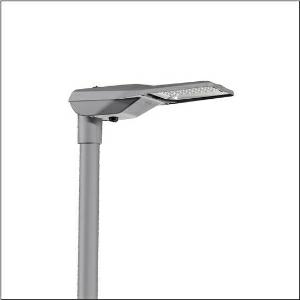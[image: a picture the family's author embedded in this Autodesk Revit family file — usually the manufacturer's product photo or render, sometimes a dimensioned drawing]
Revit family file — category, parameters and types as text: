
# Revit family: streetlight_sl_21_mini___st0_8a_5xe2c33t08hb_2b08
name_source: partatom
category: Lighting Fixtures
units: mm (PartAtom-declared; Revit-internal decimal feet)

## family parameters
Cut with Voids When Loaded = No
Host = Face
Light Source = No
Part Type = Normal
Room Calculation Point = No
Round Connector Dimension = Use Diameter
Shared = No

## types (1)
- --- (1 x LED, 9040 lm, 66 W, 3000K)
    Apparent Load = 66 VA
    CIE Flux Codes = 38 75 97 100 100
    Color Rendering = 70
    Color Temperature = 3000K
    Default Elevation = 1800 mm
    Description = Streetlight SL 21 mini, mast luminaire, primary light control with lens, of PMMA, primary optical cover: cover, of toughened safety glass, transparent, light distribution: ST0.8a, light emission: direct distribution, primary light characteristic: asymmetric, installation type: side-entry, post-top, LED, High Power LED, rated luminous flux: 9.040lm, luminous efficacy: 137lm/W, light colour: 730, colour temperature: 3000K, control gear: D4i, control: overheat protection, constant luminous flux control, time-dependent luminous flux control, flexible luminous flux parameterisation, pre-setting: logarithmic dimming characteristic, mains connection: 220..240V, AC, 50/60Hz, start of lifetime: 66W, end of service life: 69W, reduction: 30W, luminaire housing, of diecast aluminium, powder-coated, Siteco® metallic grey (DB 702S), corrosivity category C5 mid according to DIN EN ISO 12944, please order mast flange separately, inclination adjustable: 0°, 5°, 10°, 15°, sealing non-destructively replaceable, multi-level sealing system, length: 628mm, width: 235mm, height: 110mm, mast flange for spigot size: 42mm (side-entry): 5XC10008XM4, 60/48mm (side-entry/post-top): 5XC10108XM2, 76/60mm (side-entry/post-top): 5XC10108XM1, mounting height: 4..8m, Smart Interface below and above, protection rating (complete): IP66, insulation class (complete): insulation class II (safety insulation), certification: CE, ENEC, ENEC+, VDE, impact resistance: IK10, permissible operating ambient temperature for outdoor applications: -40..+50°C, standard-compliant lighting for roads and squares, packaging unit: 1 piece

Light Distribution: ST0.8a
    Height = 110 mm
    Lamp = 1 x LED
    Lamp Light Flux = 9040 lm
    Lamp Power = 66 W
    Lamp count = 1
    Length = 625 mm
    Luminous efficacy = 137 lm/W
    Manufacturer = Siteco
    ModVariant = No
    Model = 5XE2C33T08HB
    Number of Poles = 1
    OnlyDefault = Yes
    Power Factor = 1
    Product Name = Streetlight SL 21 mini | ST0.8a
    Product group = mast luminaire | pylon top
    ProductGroupID = 6100
    Protection Class = Protection class II
    Protection Degree = IP 66
    RLX_Detail_Level = 1
    RLX_Emergency_Light_Flux = 0 lm
    RLX_Emergency_Type = 0
    RLX_Emergency_Type_DB = No
    RlxData = <blob elided: 26337 chars, md5=b53643ce>
    Socket = socket
    Standby Power = 0 W
    System Light Flux = 9040 lm
    System Power = 66 W
    Type Comments = factory setting: luminous flux: 100 % | dim-lin: 254 | 670 mA
    Type Image = l_1003514.jpg
    URL = http://relux.com
    VarID = @adj_206607
    Voltage = 0 V
    Weight = 0.00 kg
    Width = 234 mm

## geometry (parser evidence)
native form markers: Blend x4, Sweep x8
no freeform markers — native parametric forms only
